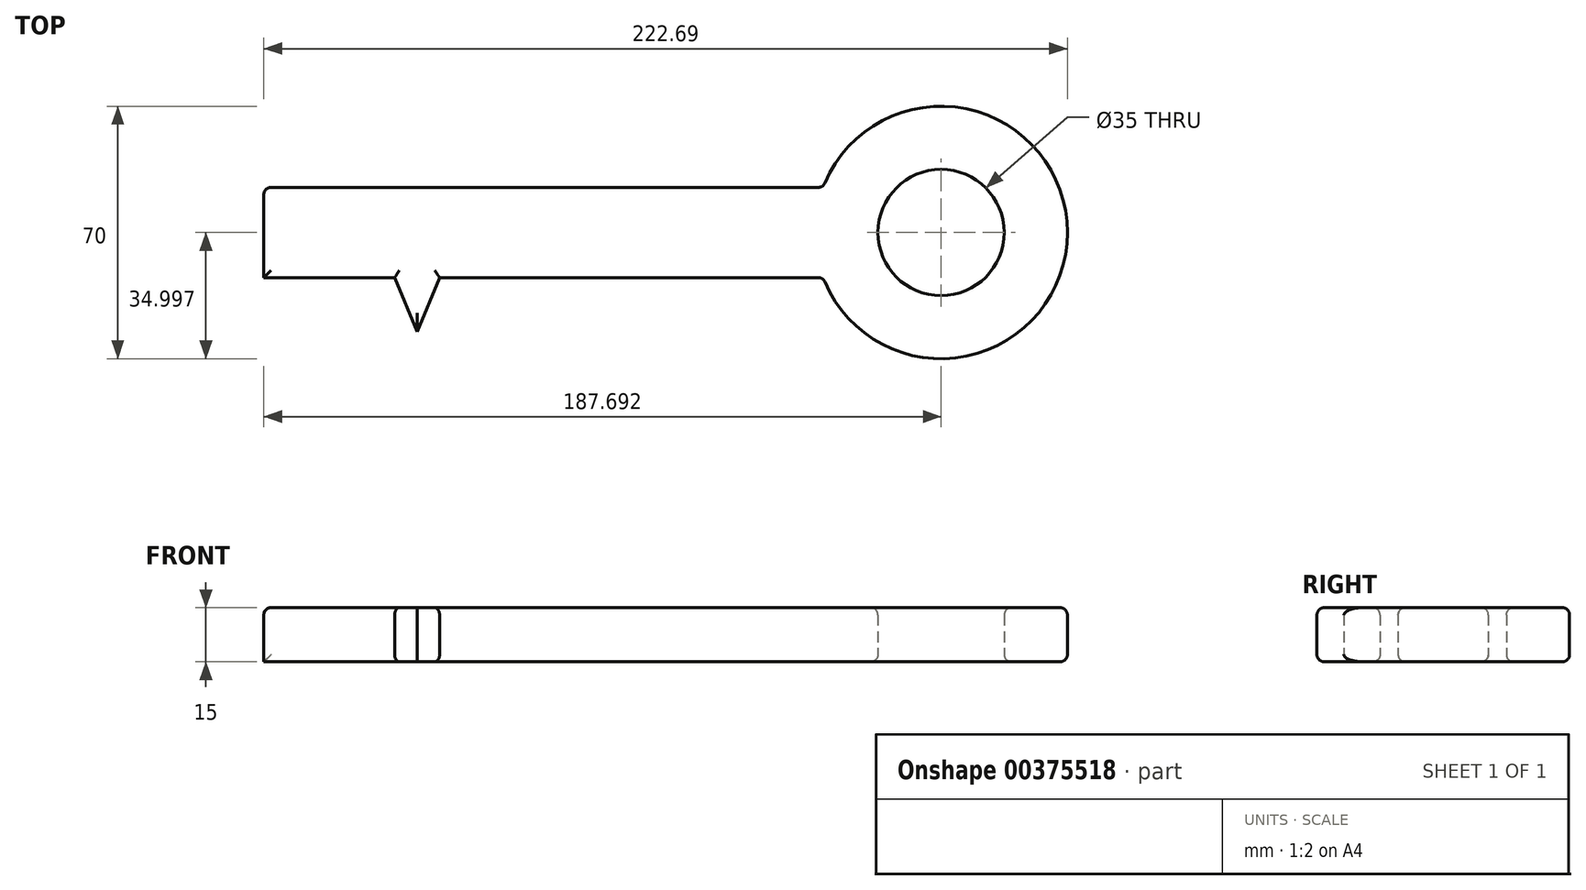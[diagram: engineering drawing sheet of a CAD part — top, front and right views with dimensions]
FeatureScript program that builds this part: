
annotation { "Feature Type Name" : "Feature", "Feature Type Description" : "" }
export const myFeature = defineFeature(function(context is Context, id is Id, definition is map)
    precondition{}
    {
        {
            var Q0;
            Q0=qCreatedBy(makeId("Top.planeOp"),FACE);
            var sketch = newSketch(context, id + "F0", { "sketchPlane" : qUnion([Q0])});
            skLineSegment(sketch, "E0.bottom", {"start": v(-129.38, 17.3) * mm, "end": v(25.62, 17.3) * mm});
            skLineSegment(sketch, "E0.top", {"start": v(-129.38, -7.7) * mm, "end": v(25.62, -7.7) * mm});
            skLineSegment(sketch, "E0.left", {"start": v(-129.38, 17.3) * mm, "end": v(-129.38, -7.7) * mm});
            skLineSegment(sketch, "E0.right", {"start": v(25.62, 17.3) * mm, "end": v(25.62, -7.7) * mm});
            skLineSegment(sketch, "E1.bottom", {"start": v(-129.38, -7.7) * mm, "end": v(-121.13, -7.7) * mm});
            skLineSegment(sketch, "E1.top", {"start": v(-129.38, -37.7) * mm, "end": v(-121.13, -37.7) * mm});
            skLineSegment(sketch, "E1.left", {"start": v(-129.38, -7.7) * mm, "end": v(-129.38, -37.7) * mm});
            skLineSegment(sketch, "E1.right", {"start": v(-121.13, -7.7) * mm, "end": v(-121.13, -37.7) * mm});
            skLineSegment(sketch, "E2.bottom", {"start": v(-111.13, -7.7) * mm, "end": v(-103.13, -7.7) * mm});
            skLineSegment(sketch, "E2.top", {"start": v(-111.13, -22.7) * mm, "end": v(-103.13, -22.7) * mm});
            skLineSegment(sketch, "E2.left", {"start": v(-111.13, -7.7) * mm, "end": v(-111.13, -22.7) * mm});
            skLineSegment(sketch, "E2.right", {"start": v(-103.13, -7.7) * mm, "end": v(-103.13, -22.7) * mm});
            skLineSegment(sketch, "E3", {"start": v(-93.13, -7.7) * mm, "end": v(-86.9, -22.7) * mm});
            skLineSegment(sketch, "E4", {"start": v(-80.67, -7.7) * mm, "end": v(-86.9, -22.7) * mm});
            skArc(sketch, "E5", {"start": v(25.62, -7.7) * mm, "mid": v(93.31, 4.8) * mm, "end": v(25.62, 17.3) * mm});
            skCircle(sketch, "E6", {"center": v(58.31, 4.8) * mm, "radius": 17.5 * mm});
            skLineSegment(sketch, "E7", {"start": v(58.31, 4.8) * mm, "end": v(-129.38, 4.8) * mm, "construction": true});
            skSolve(sketch);
        }
        {
            var Q0;
            Q0=makeQuery(id+"F0.imprint","IMPRINT",FACE,{"disambiguationData":[TD([[makeQuery(id+"F0.imprint","IMPRINT",EDGE,{"derivedFrom":sQuery(id+"F0.wireOp",EDGE,"E0.bottom")}),-1.0]])]});
            var Q1;
            Q1=makeQuery(id+"F0.imprint","IMPRINT",FACE,{"disambiguationData":[TD([[makeQuery(id+"F0.imprint","IMPRINT",EDGE,{"derivedFrom":sQuery(id+"F0.wireOp",EDGE,"E0.right")}),1.0]])]});
            var Q2;
            Q2=makeQuery(id+"F0.imprint","IMPRINT",FACE,{"disambiguationData":[TD([[makeQuery(id+"F0.imprint","IMPRINT",EDGE,{"derivedFrom":sQuery(id+"F0.wireOp",EDGE,"E1.bottom")}),-1.0]])]});
            var Q3;
            Q3=makeQuery(id+"F0.imprint","IMPRINT",FACE,{"disambiguationData":[TD([[makeQuery(id+"F0.imprint","IMPRINT",EDGE,{"derivedFrom":sQuery(id+"F0.wireOp",EDGE,"E2.bottom")}),-1.0]])]});
            var Q4;
            {var subQ0=sQuery(id+"F0.wireOp",EDGE,"E3");Q4=makeQuery(id+"F0.imprint","IMPRINT",FACE,{"disambiguationData":[TD([[makeQuery(id+"F0.imprint","IMPRINT",EDGE,{"derivedFrom":subQ0}),1.0]])]});}
            extrude(context, id + "F1", {"entities" : qUnion([Q0, Q1, Q2, Q3, Q4]), "depth" : 15 * mm});
        }
        {
            var Q0;
            Q0=makeQuery(id+"F1.opExtrude","CAP_EDGE",EDGE,{"disambiguationData":[OSD([sQuery(id+"F0.wireOp",EDGE,"E0.bottom")])],"isStart":false});
            var Q1;
            {var subQ0=sQuery(id+"F0.wireOp",EDGE,"E0.top");Q1=makeQuery(id+"F1.opExtrude","CAP_EDGE",EDGE,{"disambiguationData":[OSD([subQ0]),TDD([makeQuery(id+"F0.imprint","IMPRINT",EDGE,{"disambiguationData":[TD([[makeQuery(id+"F0.imprint","INTERSECT",VERTEX,{"derivedFrom":[subQ0,sQuery(id+"F0.wireOp",EDGE,"E4")]}),-1.0]])],"derivedFrom":subQ0})])],"isStart":false});}
            var Q2;
            Q2=makeQuery(id+"F1.opExtrude","CAP_EDGE",EDGE,{"disambiguationData":[OSD([sQuery(id+"F0.wireOp",EDGE,"E4")])],"isStart":false});
            var Q3;
            Q3=makeQuery(id+"F1.opExtrude","CAP_EDGE",EDGE,{"disambiguationData":[OSD([sQuery(id+"F0.wireOp",EDGE,"E2.right")])],"isStart":false});
            var Q4;
            {var subQ0=sQuery(id+"F0.wireOp",EDGE,"E0.top");Q4=makeQuery(id+"F1.opExtrude","CAP_EDGE",EDGE,{"disambiguationData":[OSD([subQ0]),TDD([makeQuery(id+"F0.imprint","IMPRINT",EDGE,{"disambiguationData":[TD([[makeQuery(id+"F0.imprint","INTERSECT",VERTEX,{"derivedFrom":[subQ0,sQuery(id+"F0.wireOp",EDGE,"E3")]}),1.0]])],"derivedFrom":subQ0})])],"isStart":false});}
            var Q5;
            Q5=makeQuery(id+"F1.opExtrude","CAP_EDGE",EDGE,{"disambiguationData":[OSD([sQuery(id+"F0.wireOp",EDGE,"E3")])],"isStart":false});
            var Q6;
            Q6=makeQuery(id+"F1.opExtrude","CAP_EDGE",EDGE,{"disambiguationData":[OSD([sQuery(id+"F0.wireOp",EDGE,"E2.left")])],"isStart":false});
            var Q7;
            Q7=makeQuery(id+"F1.opExtrude","CAP_EDGE",EDGE,{"disambiguationData":[OSD([sQuery(id+"F0.wireOp",EDGE,"E2.top")])],"isStart":false});
            var Q8;
            {var subQ0=sQuery(id+"F0.wireOp",EDGE,"E0.top");Q8=makeQuery(id+"F1.opExtrude","CAP_EDGE",EDGE,{"disambiguationData":[OSD([subQ0]),TDD([makeQuery(id+"F0.imprint","IMPRINT",EDGE,{"disambiguationData":[TD([[makeQuery(id+"F0.imprint","INTERSECT",VERTEX,{"derivedFrom":[subQ0,sQuery(id+"F0.wireOp",EDGE,"E1.bottom"),sQuery(id+"F0.wireOp",EDGE,"E1.right")]}),-1.0]])],"derivedFrom":subQ0})])],"isStart":false});}
            var Q9;
            Q9=makeQuery(id+"F1.opExtrude","CAP_EDGE",EDGE,{"disambiguationData":[OSD([sQuery(id+"F0.wireOp",EDGE,"E1.right")])],"isStart":false});
            var Q10;
            Q10=makeQuery(id+"F1.opExtrude","CAP_EDGE",EDGE,{"disambiguationData":[OSD([sQuery(id+"F0.wireOp",EDGE,"E1.top")])],"isStart":false});
            var Q11;
            Q11=makeQuery(id+"F1.opExtrude","CAP_EDGE",EDGE,{"disambiguationData":[OSD([sQuery(id+"F0.wireOp",EDGE,"E0.left"),sQuery(id+"F0.wireOp",EDGE,"E1.left")])],"isStart":false});
            var Q12;
            Q12=makeQuery(id+"F1.opExtrude","CAP_EDGE",EDGE,{"disambiguationData":[OSD([sQuery(id+"F0.wireOp",EDGE,"E5")])],"isStart":false});
            var Q13;
            Q13=makeQuery(id+"F1.opExtrude","CAP_EDGE",EDGE,{"disambiguationData":[OSD([sQuery(id+"F0.wireOp",EDGE,"E6")])],"isStart":false});
            var Q14;
            Q14=makeQuery(id+"F1.opExtrude","SWEPT_FACE",FACE,{"disambiguationData":[OSD([sQuery(id+"F0.wireOp",EDGE,"E5")])]});
            var Q15;
            Q15=makeQuery(id+"F1.opExtrude","SWEPT_FACE",FACE,{"disambiguationData":[OSD([sQuery(id+"F0.wireOp",EDGE,"E0.bottom")])]});
            var Q16;
            {var subQ0=sQuery(id+"F0.wireOp",EDGE,"E0.top");Q16=makeQuery(id+"F1.opExtrude","CAP_EDGE",EDGE,{"disambiguationData":[OSD([subQ0]),TDD([makeQuery(id+"F0.imprint","IMPRINT",EDGE,{"disambiguationData":[TD([[makeQuery(id+"F0.imprint","INTERSECT",VERTEX,{"derivedFrom":[subQ0,sQuery(id+"F0.wireOp",EDGE,"E1.bottom"),sQuery(id+"F0.wireOp",EDGE,"E1.right")]}),-1.0]])],"derivedFrom":subQ0})])],"isStart":true});}
            var Q17;
            Q17=makeQuery(id+"F1.opExtrude","CAP_EDGE",EDGE,{"disambiguationData":[OSD([sQuery(id+"F0.wireOp",EDGE,"E2.left")])],"isStart":true});
            var Q18;
            Q18=makeQuery(id+"F1.opExtrude","CAP_EDGE",EDGE,{"disambiguationData":[OSD([sQuery(id+"F0.wireOp",EDGE,"E1.right")])],"isStart":true});
            var Q19;
            Q19=makeQuery(id+"F1.opExtrude","CAP_EDGE",EDGE,{"disambiguationData":[OSD([sQuery(id+"F0.wireOp",EDGE,"E2.right")])],"isStart":true});
            var Q20;
            {var subQ0=sQuery(id+"F0.wireOp",EDGE,"E0.top");Q20=makeQuery(id+"F1.opExtrude","CAP_EDGE",EDGE,{"disambiguationData":[OSD([subQ0]),TDD([makeQuery(id+"F0.imprint","IMPRINT",EDGE,{"disambiguationData":[TD([[makeQuery(id+"F0.imprint","INTERSECT",VERTEX,{"derivedFrom":[subQ0,sQuery(id+"F0.wireOp",EDGE,"E3")]}),1.0]])],"derivedFrom":subQ0})])],"isStart":true});}
            var Q21;
            Q21=makeQuery(id+"F1.opExtrude","CAP_EDGE",EDGE,{"disambiguationData":[OSD([sQuery(id+"F0.wireOp",EDGE,"E3")])],"isStart":true});
            var Q22;
            {var subQ0=sQuery(id+"F0.wireOp",EDGE,"E0.top");Q22=makeQuery(id+"F1.opExtrude","CAP_EDGE",EDGE,{"disambiguationData":[OSD([subQ0]),TDD([makeQuery(id+"F0.imprint","IMPRINT",EDGE,{"disambiguationData":[TD([[makeQuery(id+"F0.imprint","INTERSECT",VERTEX,{"derivedFrom":[subQ0,sQuery(id+"F0.wireOp",EDGE,"E4")]}),-1.0]])],"derivedFrom":subQ0})])],"isStart":true});}
            var Q23;
            Q23=makeQuery(id+"F1.opExtrude","CAP_EDGE",EDGE,{"disambiguationData":[OSD([sQuery(id+"F0.wireOp",EDGE,"E2.top")])],"isStart":true});
            var Q24;
            Q24=makeQuery(id+"F1.opExtrude","CAP_EDGE",EDGE,{"disambiguationData":[OSD([sQuery(id+"F0.wireOp",EDGE,"E4")])],"isStart":true});
            var Q25;
            Q25=makeQuery(id+"F1.opExtrude","CAP_EDGE",EDGE,{"disambiguationData":[OSD([sQuery(id+"F0.wireOp",EDGE,"E5")])],"isStart":true});
            var Q26;
            Q26=makeQuery(id+"F1.opExtrude","CAP_EDGE",EDGE,{"disambiguationData":[OSD([sQuery(id+"F0.wireOp",EDGE,"E6")])],"isStart":true});
            fillet(context, id + "F2", {"entities" : qUnion([Q0, Q1, Q2, Q3, Q4, Q5, Q6, Q7, Q8, Q9, Q10, Q11, Q12, Q13, Q14, Q15, Q16, Q17, Q18, Q19, Q20, Q21, Q22, Q23, Q24, Q25, Q26]), "radius" : 2 * mm, "tangentPropagation" : true, "allowEdgeOverflow" : false});
        }
    });
